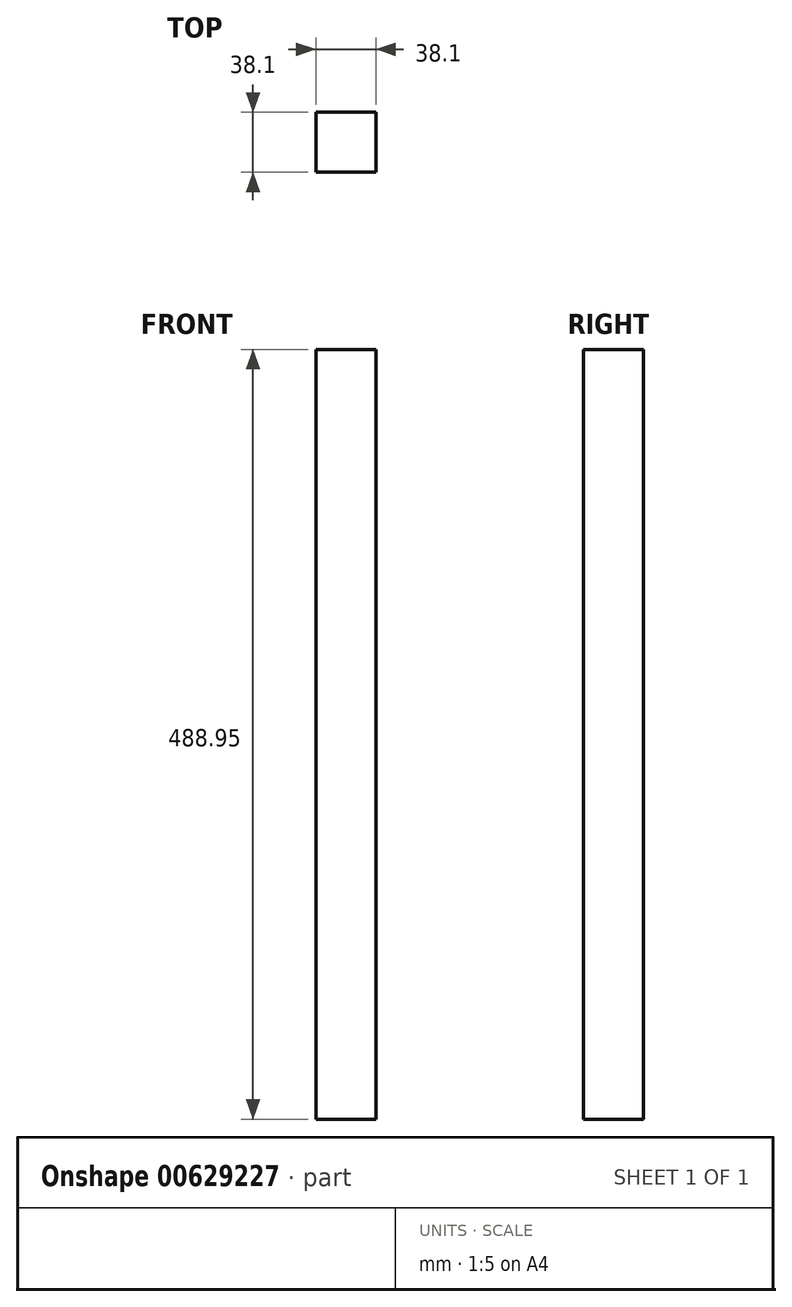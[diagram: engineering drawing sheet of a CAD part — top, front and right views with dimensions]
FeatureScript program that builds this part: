
annotation { "Feature Type Name" : "Feature", "Feature Type Description" : "" }
export const myFeature = defineFeature(function(context is Context, id is Id, definition is map)
    precondition{}
    {
        {
            var Q0;
            Q0=qCreatedBy(makeId("Top.planeOp"),FACE);
            var sketch = newSketch(context, id + "F0", { "sketchPlane" : qUnion([Q0])});
            skLineSegment(sketch, "E0.bottom", {"start": v(0, 0) * mm, "end": v(-38.1, 0) * mm});
            skLineSegment(sketch, "E0.top", {"start": v(0, -38.1) * mm, "end": v(-38.1, -38.1) * mm});
            skLineSegment(sketch, "E0.left", {"start": v(0, 0) * mm, "end": v(0, -38.1) * mm});
            skLineSegment(sketch, "E0.right", {"start": v(-38.1, 0) * mm, "end": v(-38.1, -38.1) * mm});
            skSolve(sketch);
        }
        {
            var Q0;
            Q0=makeQuery(id+"F0.imprint","IMPRINT",FACE,{"disambiguationData":[TD([[makeQuery(id+"F0.imprint","IMPRINT",EDGE,{"derivedFrom":sQuery(id+"F0.wireOp",EDGE,"E0.bottom")}),1.0]])]});
            extrude(context, id + "F1", {"entities" : qUnion([Q0]), "oppositeDirection" : true, "depth" : 488.95 * mm, "offsetDistance" : 25.4 * mm});
        }
    });
